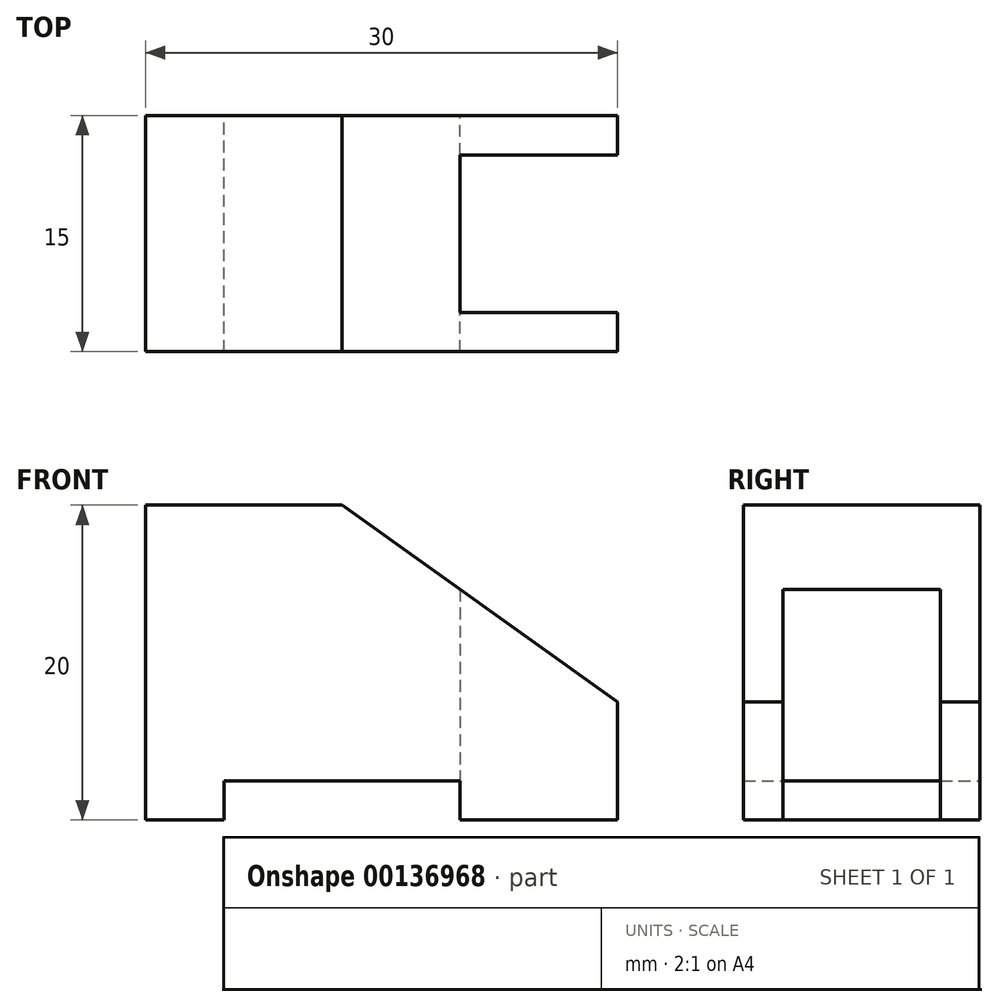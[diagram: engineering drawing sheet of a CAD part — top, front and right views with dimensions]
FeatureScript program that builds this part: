
annotation { "Feature Type Name" : "Feature", "Feature Type Description" : "" }
export const myFeature = defineFeature(function(context is Context, id is Id, definition is map)
    precondition{}
    {
        {
            var Q0;
            Q0=qCreatedBy(makeId("Front.planeOp"),FACE);
            var sketch = newSketch(context, id + "F0", { "sketchPlane" : qUnion([Q0])});
            skLineSegment(sketch, "E0", {"start": v(0, 20) * mm, "end": v(0, 0) * mm});
            skLineSegment(sketch, "E1", {"start": v(0, 0) * mm, "end": v(5, 0) * mm});
            skLineSegment(sketch, "E2", {"start": v(5, 0) * mm, "end": v(5, 2.5) * mm});
            skLineSegment(sketch, "E3", {"start": v(5, 2.5) * mm, "end": v(20, 2.5) * mm});
            skLineSegment(sketch, "E4", {"start": v(20, 2.5) * mm, "end": v(20, 0) * mm});
            skLineSegment(sketch, "E5", {"start": v(20, 0) * mm, "end": v(30, 0) * mm});
            skLineSegment(sketch, "E6", {"start": v(30, 0) * mm, "end": v(30, 7.5) * mm});
            skLineSegment(sketch, "E7", {"start": v(30, 7.5) * mm, "end": v(12.5, 20) * mm});
            skLineSegment(sketch, "E8", {"start": v(12.5, 20) * mm, "end": v(0, 20) * mm});
            skSolve(sketch);
        }
        {
            var Q0;
            Q0 = qSketchRegion(id + "F0", true);
            extrude(context, id + "F1", {"entities" : qUnion([Q0]), "depth" : 15 * mm});
        }
        {
            var Q0;
            Q0=makeQuery(id+"F1.opExtrude","SWEPT_FACE",FACE,{"disambiguationData":[OSD([sQuery(id+"F0.wireOp",EDGE,"E5")])]});
            var sketch = newSketch(context, id + "F2", { "sketchPlane" : qUnion([Q0])});
            skLineSegment(sketch, "E9", {"start": v(30, 12.5) * mm, "end": v(30, 2.5) * mm});
            skLineSegment(sketch, "E10", {"start": v(30, 12.5) * mm, "end": v(20, 12.5) * mm});
            skLineSegment(sketch, "E11", {"start": v(20, 12.5) * mm, "end": v(20, 2.5) * mm});
            skLineSegment(sketch, "E12", {"start": v(20, 2.5) * mm, "end": v(30, 2.5) * mm});
            skSolve(sketch);
        }
        {
            var Q0;
            Q0 = qSketchRegion(id + "F2", true);
            extrude(context, id + "F3", {"entities" : qUnion([Q0]), "operationType" : NewBodyOperationType.REMOVE, "endBound" : BoundingType.THROUGH_ALL, "oppositeDirection" : true, "depth" : 25 * mm});
        }
    });
